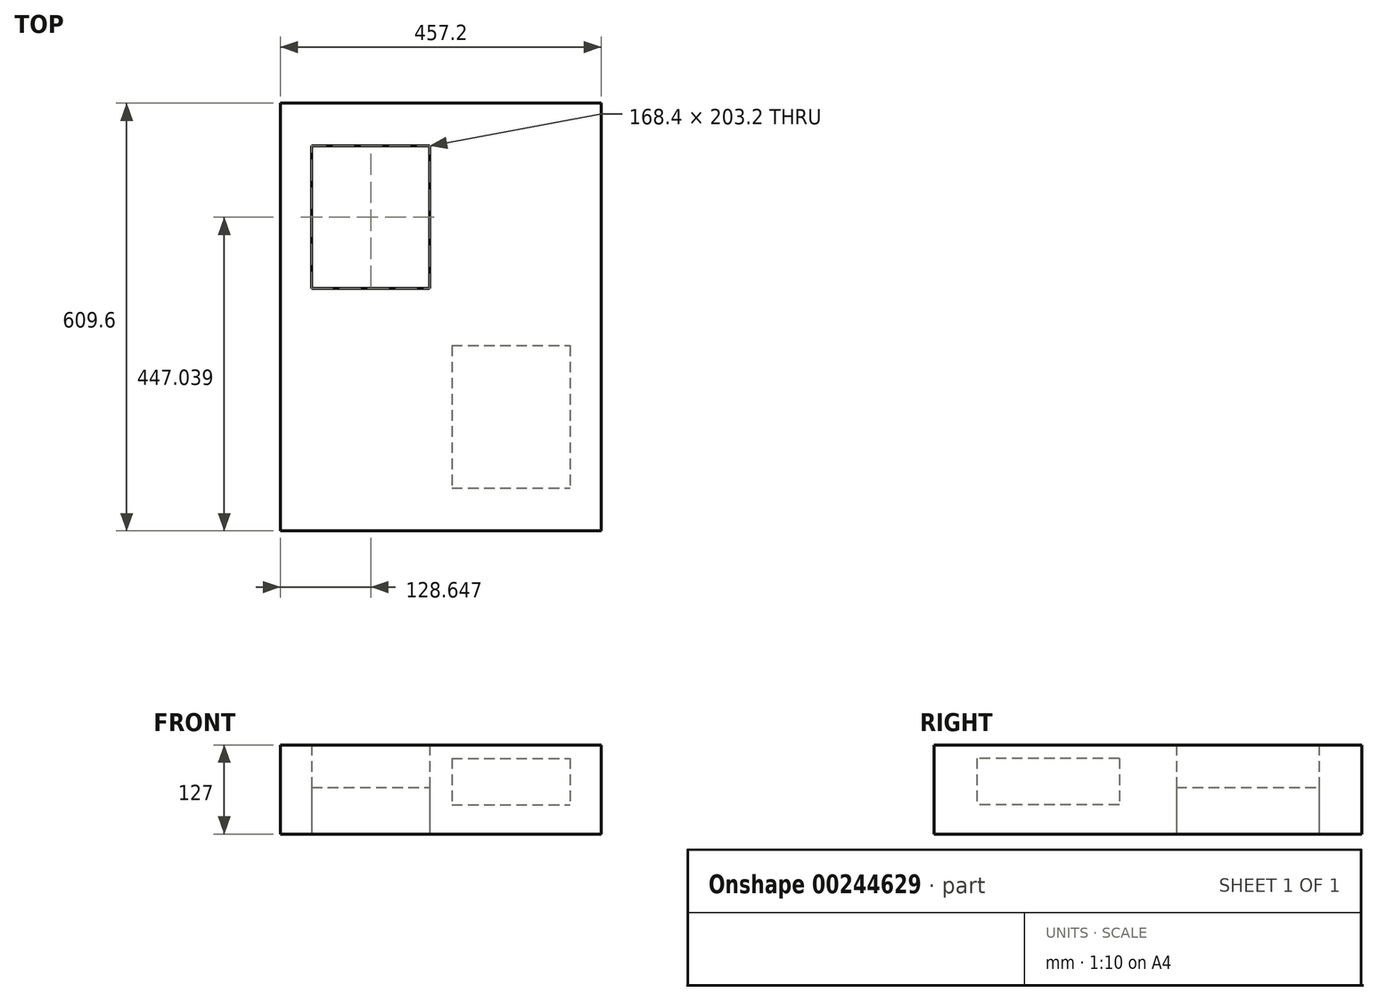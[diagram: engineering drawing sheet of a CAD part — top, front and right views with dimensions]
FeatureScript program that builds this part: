
annotation { "Feature Type Name" : "Feature", "Feature Type Description" : "" }
export const myFeature = defineFeature(function(context is Context, id is Id, definition is map)
    precondition{}
    {
        {
            var Q0;
            Q0=qCreatedBy(makeId("Top.planeOp"),FACE);
            var sketch = newSketch(context, id + "F0", { "sketchPlane" : qUnion([Q0])});
            skLineSegment(sketch, "E0.bottom", {"start": v(-240.8, 322.77) * mm, "end": v(216.4, 322.77) * mm});
            skLineSegment(sketch, "E0.top", {"start": v(-240.8, -286.83) * mm, "end": v(216.4, -286.83) * mm});
            skLineSegment(sketch, "E0.left", {"start": v(-240.8, 322.77) * mm, "end": v(-240.8, -286.83) * mm});
            skLineSegment(sketch, "E0.right", {"start": v(216.4, 322.77) * mm, "end": v(216.4, -286.83) * mm});
            skLineSegment(sketch, "E1.bottom", {"start": v(-196.34, 58.6) * mm, "end": v(-27.94, 58.6) * mm});
            skLineSegment(sketch, "E1.top", {"start": v(-196.34, 261.8) * mm, "end": v(-27.94, 261.8) * mm});
            skLineSegment(sketch, "E1.left", {"start": v(-196.34, 58.6) * mm, "end": v(-196.34, 261.8) * mm});
            skLineSegment(sketch, "E1.right", {"start": v(-27.94, 58.6) * mm, "end": v(-27.94, 261.8) * mm});
            skSolve(sketch);
        }
        {
            var Q0;
            Q0=qCreatedBy(makeId("Top.planeOp"),FACE);
            cPlane(context, id + "F1", {"entities" : qUnion([Q0]), "cplaneType" : CPlaneType.OFFSET, "offset" : 41.66 * mm, "width" : 152.4 * mm, "height" : 152.4 * mm});
        }
        {
            var Q0;
            Q0=qCreatedBy(id+"F1.planeOp",FACE);
            var sketch = newSketch(context, id + "F2", { "sketchPlane" : qUnion([Q0])});
            skLineSegment(sketch, "E2.bottom", {"start": v(3.55, -22.67) * mm, "end": v(171.96, -22.67) * mm});
            skLineSegment(sketch, "E2.top", {"start": v(3.55, -225.87) * mm, "end": v(171.96, -225.87) * mm});
            skLineSegment(sketch, "E2.left", {"start": v(3.55, -22.67) * mm, "end": v(3.55, -225.87) * mm});
            skLineSegment(sketch, "E2.right", {"start": v(171.96, -22.67) * mm, "end": v(171.96, -225.87) * mm});
            skSolve(sketch);
        }
        {
            var Q0;
            Q0=makeQuery(id+"F0.imprint","IMPRINT",FACE,{"disambiguationData":[TD([[makeQuery(id+"F0.imprint","IMPRINT",EDGE,{"derivedFrom":sQuery(id+"F0.wireOp",EDGE,"E1.bottom")}),1.0]])]});
            var Q1;
            Q1=makeQuery(id+"F2.imprint","IMPRINT",FACE,{"disambiguationData":[TD([[makeQuery(id+"F2.imprint","IMPRINT",EDGE,{"derivedFrom":sQuery(id+"F2.wireOp",EDGE,"E2.bottom")}),-1.0]])]});
            extrude(context, id + "F3", {"entities" : qUnion([Q0, Q1]), "depth" : 66.3 * mm, "offsetDistance" : 25.4 * mm});
        }
        {
            var Q0;
            Q0=makeQuery(id+"F0.imprint","IMPRINT",FACE,{"disambiguationData":[TD([[makeQuery(id+"F0.imprint","IMPRINT",EDGE,{"derivedFrom":sQuery(id+"F0.wireOp",EDGE,"E0.bottom")}),-1.0]])]});
            extrude(context, id + "F4", {"entities" : qUnion([Q0]), "depth" : 127 * mm, "offsetDistance" : 25.4 * mm});
        }
    });
